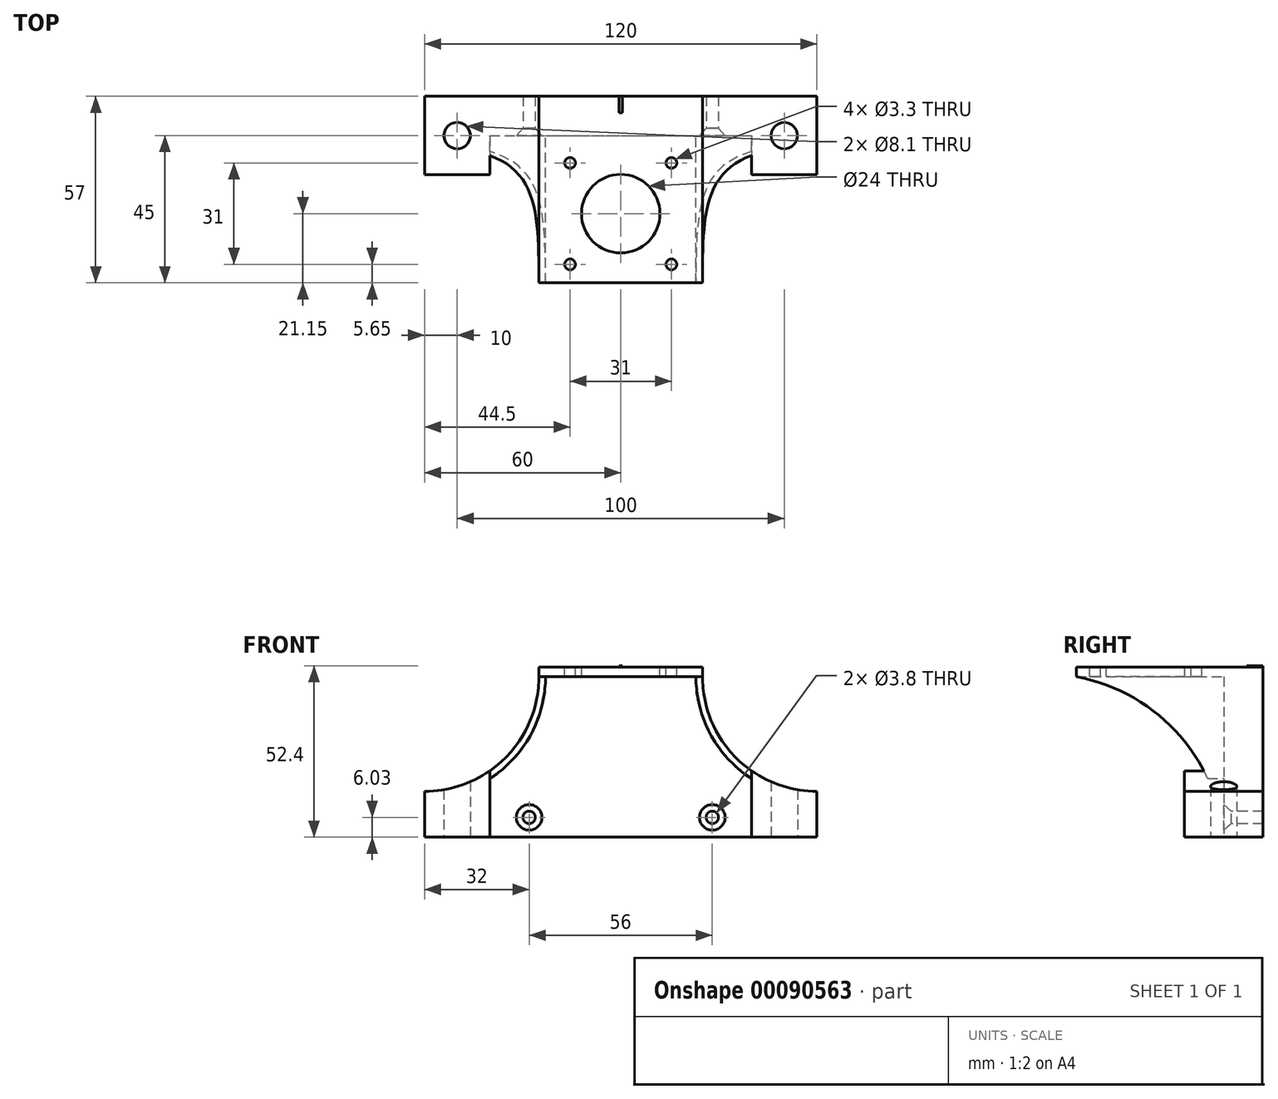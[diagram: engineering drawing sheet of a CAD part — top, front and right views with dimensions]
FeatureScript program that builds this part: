
annotation { "Feature Type Name" : "Feature", "Feature Type Description" : "" }
export const myFeature = defineFeature(function(context is Context, id is Id, definition is map)
    precondition{}
    {
        {
            var Q0;
            Q0=qCreatedBy(makeId("Front.planeOp"),FACE);
            var sketch = newSketch(context, id + "F0", { "sketchPlane" : qUnion([Q0])});
            skLineSegment(sketch, "E0.bottom", {"start": v(-27.18, 22.72) * mm, "end": v(22.82, 22.72) * mm});
            skLineSegment(sketch, "E0.top", {"start": v(-62.18, -29.28) * mm, "end": v(57.82, -29.28) * mm});
            skLineSegment(sketch, "E0.right", {"start": v(57.82, -15.28) * mm, "end": v(57.82, -29.28) * mm});
            skPoint(sketch, "E1", {"position": v(-2.18, 22.72) * mm});
            skLineSegment(sketch, "E2.top", {"start": v(-27.18, 19.72) * mm, "end": v(22.82, 19.72) * mm});
            skLineSegment(sketch, "E2.left", {"start": v(-27.18, 22.72) * mm, "end": v(-27.18, 19.72) * mm});
            skLineSegment(sketch, "E2.right", {"start": v(22.82, 22.72) * mm, "end": v(22.82, 19.72) * mm});
            skLineSegment(sketch, "E3", {"start": v(-62.18, -15.28) * mm, "end": v(57.82, -15.28) * mm, "construction": true});
            skArc(sketch, "E4", {"start": v(-62.18, -15.28) * mm, "mid": v(-37.43, -5.03) * mm, "end": v(-27.18, 19.72) * mm});
            skArc(sketch, "E5", {"start": v(22.82, 19.72) * mm, "mid": v(33.07, -5.03) * mm, "end": v(57.82, -15.28) * mm});
            skLineSegment(sketch, "E6.trimOffspring", {"start": v(-62.18, -15.28) * mm, "end": v(-62.18, -29.28) * mm});
            skPoint(sketch, "E0.left.start.orphan", {"position": v(-62.18, 22.72) * mm});
            skPoint(sketch, "E7.orphan", {"position": v(57.82, 22.72) * mm});
            skSolve(sketch);
        }
        {
            var Q0;
            Q0=makeQuery(id+"F0.imprint","IMPRINT",FACE,{"disambiguationData":[TD([[makeQuery(id+"F0.imprint","IMPRINT",EDGE,{"derivedFrom":sQuery(id+"F0.wireOp",EDGE,"E0.top")}),1.0]])]});
            var Q1;
            Q1=makeQuery(id+"F0.imprint","IMPRINT",FACE,{"disambiguationData":[TD([[makeQuery(id+"F0.imprint","IMPRINT",EDGE,{"derivedFrom":sQuery(id+"F0.wireOp",EDGE,"E0.bottom")}),-1.0]])]});
            extrude(context, id + "F1", {"entities" : qUnion([Q0, Q1]), "depth" : 12 * mm});
        }
        {
            var Q0;
            Q0=makeQuery(id+"F1.opExtrude","CAP_FACE",FACE,{"disambiguationData":[OSD([sQuery(id+"F0.wireOp",EDGE,"E0.top"),sQuery(id+"F0.wireOp",EDGE,"E0.right"),sQuery(id+"F0.wireOp",EDGE,"E0.bottom"),sQuery(id+"F0.wireOp",EDGE,"E2.left"),sQuery(id+"F0.wireOp",EDGE,"E2.right"),sQuery(id+"F0.wireOp",EDGE,"E4"),sQuery(id+"F0.wireOp",EDGE,"E5"),sQuery(id+"F0.wireOp",EDGE,"E6.trimOffspring")])],"isStart":false});
            var sketch = newSketch(context, id + "F2", { "sketchPlane" : qUnion([Q0])});
            skLineSegment(sketch, "E8", {"start": v(-27.18, 19.72) * mm, "end": v(22.82, 19.72) * mm});
            skArc(sketch, "E9.0", {"start": v(-60.18, -17.22) * mm, "mid": v(-35.32, -5.72) * mm, "end": v(-25.18, 19.72) * mm});
            skArc(sketch, "E10.0", {"start": v(20.82, 19.72) * mm, "mid": v(30.96, -5.72) * mm, "end": v(55.82, -17.22) * mm});
            skLineSegment(sketch, "E11.0", {"start": v(-60.18, -17.22) * mm, "end": v(-60.18, -29.28) * mm});
            skLineSegment(sketch, "E12.0", {"start": v(55.82, -17.22) * mm, "end": v(55.82, -29.28) * mm});
            skSolve(sketch);
        }
        {
            var Q0;
            Q0=qSketchRegion(id+"F2",true);
            var Q1;
            {var subQ2=sQuery(id+"F2.wireOp",EDGE,"E9.0");Q1=makeQuery(id+"F2.imprint","IMPRINT",FACE,{"disambiguationData":[TD([[makeQuery(id+"F2.imprint","IMPRINT",EDGE,{"derivedFrom":subQ2}),1.0]])]});}
            var Q2;
            Q2=makeQuery(id+"F2.imprint","IMPRINT",FACE,{"disambiguationData":[TD([[makeQuery(id+"F2.imprint","IMPRINT",EDGE,{"derivedFrom":makeQuery(id+"F1.opExtrude","CAP_EDGE",EDGE,{"disambiguationData":[OSD([sQuery(id+"F0.wireOp",EDGE,"E0.bottom")])],"isStart":false})}),-1.0]])]});
            var Q3;
            {var subQ2=sQuery(id+"F2.wireOp",EDGE,"E10.0");Q3=makeQuery(id+"F2.imprint","IMPRINT",FACE,{"disambiguationData":[TD([[makeQuery(id+"F2.imprint","IMPRINT",EDGE,{"derivedFrom":subQ2}),1.0]])]});}
            extrude(context, id + "F3", {"entities" : qUnion([Q0, Q1, Q2, Q3]), "operationType" : NewBodyOperationType.ADD, "depth" : 45 * mm});
        }
        {
            var Q0;
            {var subQ0=sQuery(id+"F0.wireOp",EDGE,"E6.trimOffspring");Q0=makeQuery(id+"F3.boolean.opBoolean","MERGE",FACE,{"derivedFrom":[makeQuery(id+"F1.opExtrude","SWEPT_FACE",FACE,{"disambiguationData":[OSD([subQ0])]}),makeQuery(id+"F3.opExtrude","SWEPT_FACE",FACE,{"disambiguationData":[OSD([subQ0])]})]});}
            var sketch = newSketch(context, id + "F4", { "sketchPlane" : qUnion([Q0])});
            skPoint(sketch, "E13.0", {"position": v(57, 19.72) * mm});
            skPoint(sketch, "E14.0", {"position": v(12, -29.28) * mm});
            skArc(sketch, "E15", {"start": v(57, 19.72) * mm, "mid": v(26.33, 2.73) * mm, "end": v(12, -29.28) * mm});
            skLineSegment(sketch, "E16.0", {"start": v(57, -15.28) * mm, "end": v(57, 19.72) * mm});
            skLineSegment(sketch, "E17.0", {"start": v(57, -15.28) * mm, "end": v(57, -29.28) * mm});
            skLineSegment(sketch, "E18.0", {"start": v(57, -29.28) * mm, "end": v(0, -29.28) * mm});
            skSolve(sketch);
        }
        {
            var Q0;
            Q0=qSketchRegion(id+"F4",true);
            extrude(context, id + "F5", {"entities" : qUnion([Q0]), "operationType" : NewBodyOperationType.REMOVE, "endBound" : BoundingType.THROUGH_ALL, "oppositeDirection" : true, "depth" : 25 * mm});
        }
        {
            var Q0;
            {var subQ0=sQuery(id+"F0.wireOp",EDGE,"E0.bottom");Q0=makeQuery(id+"F3.boolean.opBoolean","MERGE",FACE,{"derivedFrom":[makeQuery(id+"F1.opExtrude","SWEPT_FACE",FACE,{"disambiguationData":[OSD([subQ0])]}),makeQuery(id+"F3.opExtrude","SWEPT_FACE",FACE,{"disambiguationData":[OSD([subQ0])]})]});}
            var sketch = newSketch(context, id + "F6", { "sketchPlane" : qUnion([Q0])});
            skLineSegment(sketch, "E19", {"start": v(-2.18, -57) * mm, "end": v(-2.18, 0) * mm, "construction": true});
            skLineSegment(sketch, "E20", {"start": v(-27.18, -35.85) * mm, "end": v(22.82, -35.85) * mm, "construction": true});
            skCircle(sketch, "E21", {"center": v(-2.18, -35.85) * mm, "radius": 12 * mm});
            skLineSegment(sketch, "E22", {"start": v(-27.18, -51.35) * mm, "end": v(22.82, -51.35) * mm, "construction": true});
            skLineSegment(sketch, "E23", {"start": v(-17.68, 0) * mm, "end": v(-17.68, -57) * mm, "construction": true});
            skCircle(sketch, "E24", {"center": v(-17.68, -51.35) * mm, "radius": 1.65 * mm});
            skCircle(sketch, "E25.0.1.0", {"center": v(-17.68, -20.35) * mm, "radius": 1.65 * mm});
            skCircle(sketch, "E25.1.0.0", {"center": v(13.32, -51.35) * mm, "radius": 1.65 * mm});
            skCircle(sketch, "E25.1.1.0", {"center": v(13.32, -20.35) * mm, "radius": 1.65 * mm});
            skLineSegment(sketch, "E25.direction1", {"start": v(-17.68, -51.35) * mm, "end": v(13.32, -51.35) * mm, "construction": true});
            skLineSegment(sketch, "E25.direction2", {"start": v(-17.68, -51.35) * mm, "end": v(-17.68, -20.35) * mm, "construction": true});
            skSolve(sketch);
        }
        {
            var Q0;
            Q0=qSketchRegion(id+"F6",true);
            extrude(context, id + "F7", {"entities" : qUnion([Q0]), "operationType" : NewBodyOperationType.REMOVE, "oppositeDirection" : true, "depth" : 25 * mm});
        }
        {
            var Q0;
            Q0=makeQuery(id+"F1.opExtrude","CAP_FACE",FACE,{"disambiguationData":[OSD([sQuery(id+"F0.wireOp",EDGE,"E0.top"),sQuery(id+"F0.wireOp",EDGE,"E0.right"),sQuery(id+"F0.wireOp",EDGE,"E0.bottom"),sQuery(id+"F0.wireOp",EDGE,"E2.left"),sQuery(id+"F0.wireOp",EDGE,"E2.right"),sQuery(id+"F0.wireOp",EDGE,"E4"),sQuery(id+"F0.wireOp",EDGE,"E5"),sQuery(id+"F0.wireOp",EDGE,"E6.trimOffspring")])],"isStart":false});
            var sketch = newSketch(context, id + "F8", { "sketchPlane" : qUnion([Q0])});
            skLineSegment(sketch, "E26", {"start": v(-60.18, -23.25) * mm, "end": v(55.82, -23.25) * mm, "construction": true});
            skLineSegment(sketch, "E27", {"start": v(-30.18, -23.25) * mm, "end": v(-30.18, -29.28) * mm, "construction": true});
            skLineSegment(sketch, "E28", {"start": v(25.82, -23.25) * mm, "end": v(25.82, -29.28) * mm, "construction": true});
            skPoint(sketch, "E29", {"position": v(-30.18, -23.25) * mm});
            skPoint(sketch, "E30", {"position": v(25.82, -23.25) * mm});
            skSolve(sketch);
        }
        {
            var Q0;
            Q0=sQuery(id+"F8.wireOp",VERTEX,"E29");
            var Q1;
            Q1=sQuery(id+"F8.wireOp",VERTEX,"E30");
            var Q2;
            Q2=makeQuery(id+"F1.opExtrude","SWEPT_BODY",BODY,{"disambiguationData":[OSD([sQuery(id+"F0.wireOp",EDGE,"E0.top"),sQuery(id+"F0.wireOp",EDGE,"E0.right"),sQuery(id+"F0.wireOp",EDGE,"E0.bottom"),sQuery(id+"F0.wireOp",EDGE,"E2.left"),sQuery(id+"F0.wireOp",EDGE,"E2.right"),sQuery(id+"F0.wireOp",EDGE,"E4"),sQuery(id+"F0.wireOp",EDGE,"E5"),sQuery(id+"F0.wireOp",EDGE,"E6.trimOffspring")])]});
            hole(context, id + "F9", {"style" : HoleStyle.C_SINK, "endStyle" : HoleEndStyle.THROUGH, "standardTappedOrClearance" : lookupTablePath({ "standard" : "ANSI", "fit" : "Normal (ASME)", "size" : "#6", "type" : "Clearance" }), "standardBlindInLast" : lookupTablePath({ "fit" : "Free", "standard" : "ANSI", "size" : "#6", "type" : "Clearance" }), "holeDiameter" : 3.8 * mm, "cSinkDiameter" : 7.8 * mm, "cSinkAngle" : 82 * degree, "locations" : qUnion([Q0, Q1]), "scope" : qUnion([Q2]), "isTappedThrough" : true});
        }
        {
            var Q0;
            {var subQ0=sQuery(id+"F0.wireOp",EDGE,"E0.bottom");Q0=makeQuery(id+"F3.boolean.opBoolean","MERGE",FACE,{"derivedFrom":[makeQuery(id+"F1.opExtrude","SWEPT_FACE",FACE,{"disambiguationData":[OSD([subQ0])]}),makeQuery(id+"F3.opExtrude","SWEPT_FACE",FACE,{"disambiguationData":[OSD([subQ0])]})]});}
            var sketch = newSketch(context, id + "F10", { "sketchPlane" : qUnion([Q0])});
            skPoint(sketch, "E31", {"position": v(-2.18, 0) * mm});
            skLineSegment(sketch, "E32.bottom", {"start": v(-2.68, -5) * mm, "end": v(-1.68, -5) * mm});
            skLineSegment(sketch, "E32.top", {"start": v(-2.68, 0) * mm, "end": v(-1.68, 0) * mm});
            skLineSegment(sketch, "E32.left", {"start": v(-2.68, -5) * mm, "end": v(-2.68, 0) * mm});
            skLineSegment(sketch, "E32.right", {"start": v(-1.68, -5) * mm, "end": v(-1.68, 0) * mm});
            skPoint(sketch, "E33", {"position": v(-2.18, -5) * mm});
            skSolve(sketch);
        }
        {
            var Q0;
            Q0=qSketchRegion(id+"F10",true);
            extrude(context, id + "F11", {"entities" : qUnion([Q0]), "operationType" : NewBodyOperationType.ADD, "depth" : 0.4 * mm});
        }
        {
            var Q0;
            {var subQ0=sQuery(id+"F0.wireOp",EDGE,"E0.top");var subQ1=makeQuery(id+"F1.opExtrude","CAP_EDGE",EDGE,{"disambiguationData":[OSD([subQ0])],"isStart":false});Q0=makeQuery(id+"F3.boolean.opBoolean","MERGE",FACE,{"derivedFrom":[makeQuery(id+"F1.opExtrude","SWEPT_FACE",FACE,{"disambiguationData":[OSD([subQ0])]}),makeQuery(id+"F3.opExtrude","SWEPT_FACE",FACE,{"disambiguationData":[OSD([subQ0]),TDD([makeQuery(id+"F2.imprint","IMPRINT",EDGE,{"disambiguationData":[TD([[makeQuery(id+"F2.imprint","INTERSECT",VERTEX,{"derivedFrom":[subQ1,makeQuery(id+"F1.opExtrude","CAP_EDGE",EDGE,{"disambiguationData":[OSD([sQuery(id+"F0.wireOp",EDGE,"E6.trimOffspring")])],"isStart":false})]}),-1.0]])],"derivedFrom":subQ1})])]}),makeQuery(id+"F3.opExtrude","SWEPT_FACE",FACE,{"disambiguationData":[OSD([subQ0]),TDD([makeQuery(id+"F2.imprint","IMPRINT",EDGE,{"disambiguationData":[TD([[makeQuery(id+"F2.imprint","INTERSECT",VERTEX,{"derivedFrom":[subQ1,makeQuery(id+"F1.opExtrude","CAP_EDGE",EDGE,{"disambiguationData":[OSD([sQuery(id+"F0.wireOp",EDGE,"E0.right")])],"isStart":false})]}),1.0]])],"derivedFrom":subQ1})])]})]});}
            var sketch = newSketch(context, id + "F12", { "sketchPlane" : qUnion([Q0])});
            skLineSegment(sketch, "E34", {"start": v(-52.18, 0) * mm, "end": v(-52.18, 12) * mm, "construction": true});
            skLineSegment(sketch, "E35", {"start": v(47.82, 0) * mm, "end": v(47.82, 12) * mm, "construction": true});
            skLineSegment(sketch, "E36.bottom", {"start": v(-62.18, 0) * mm, "end": v(-42.18, 0) * mm});
            skLineSegment(sketch, "E36.top", {"start": v(-62.18, 24) * mm, "end": v(-42.18, 24) * mm});
            skLineSegment(sketch, "E36.left", {"start": v(-62.18, 0) * mm, "end": v(-62.18, 24) * mm});
            skLineSegment(sketch, "E36.right", {"start": v(-42.18, 0) * mm, "end": v(-42.18, 24) * mm});
            skCircle(sketch, "E37", {"center": v(-52.18, 12) * mm, "radius": 4.05 * mm});
            skLineSegment(sketch, "E38.bottom", {"start": v(57.82, 0) * mm, "end": v(37.82, 0) * mm});
            skLineSegment(sketch, "E38.top", {"start": v(57.82, 24) * mm, "end": v(37.82, 24) * mm});
            skLineSegment(sketch, "E38.left", {"start": v(57.82, 0) * mm, "end": v(57.82, 24) * mm});
            skLineSegment(sketch, "E38.right", {"start": v(37.82, 0) * mm, "end": v(37.82, 24) * mm});
            skCircle(sketch, "E39", {"center": v(47.82, 12) * mm, "radius": 4.05 * mm});
            skSolve(sketch);
        }
        {
            var Q0;
            {var subQ6=sQuery(id+"F12.wireOp",EDGE,"E36.top");Q0=makeQuery(id+"F12.imprint","IMPRINT",FACE,{"disambiguationData":[TD([[makeQuery(id+"F12.imprint","IMPRINT",EDGE,{"derivedFrom":subQ6}),-1.0]])]});}
            var Q1;
            {var subQ0=sQuery(id+"F12.wireOp",EDGE,"E37");var subQ1=makeQuery(id+"F1.opExtrude","CAP_EDGE",EDGE,{"disambiguationData":[OSD([sQuery(id+"F0.wireOp",EDGE,"E0.top")])],"isStart":false});var subQ2=makeQuery(id+"F12.imprint","INTERSECT",VERTEX,{"disambiguationData":[OD(0.0)],"derivedFrom":[subQ1,subQ0]});Q1=makeQuery(id+"F12.imprint","IMPRINT",FACE,{"disambiguationData":[TD([[makeQuery(id+"F12.imprint","IMPRINT",EDGE,{"disambiguationData":[TD([[subQ2,1.0]])],"derivedFrom":subQ0}),1.0]])]});}
            var Q2;
            {var subQ0=sQuery(id+"F0.wireOp",EDGE,"E4");Q2=makeQuery(id+"F3.boolean.opBoolean","MERGE",FACE,{"derivedFrom":[makeQuery(id+"F1.opExtrude","SWEPT_FACE",FACE,{"disambiguationData":[OSD([subQ0])]}),makeQuery(id+"F3.opExtrude","SWEPT_FACE",FACE,{"disambiguationData":[OSD([subQ0])]})]});}
            extrude(context, id + "F13", {"entities" : qUnion([Q0, Q1]), "operationType" : NewBodyOperationType.ADD, "endBound" : BoundingType.UP_TO_SURFACE, "oppositeDirection" : true, "endBoundEntityFace" : qUnion([Q2]), "depth" : 25 * mm});
        }
        {
            var Q0;
            {var subQ6=sQuery(id+"F12.wireOp",EDGE,"E38.top");Q0=makeQuery(id+"F12.imprint","IMPRINT",FACE,{"disambiguationData":[TD([[makeQuery(id+"F12.imprint","IMPRINT",EDGE,{"derivedFrom":subQ6}),1.0]])]});}
            var Q1;
            {var subQ0=sQuery(id+"F12.wireOp",EDGE,"E39");var subQ1=makeQuery(id+"F1.opExtrude","CAP_EDGE",EDGE,{"disambiguationData":[OSD([sQuery(id+"F0.wireOp",EDGE,"E0.top")])],"isStart":false});var subQ2=makeQuery(id+"F12.imprint","INTERSECT",VERTEX,{"disambiguationData":[OD(0.0)],"derivedFrom":[subQ1,subQ0]});Q1=makeQuery(id+"F12.imprint","IMPRINT",FACE,{"disambiguationData":[TD([[makeQuery(id+"F12.imprint","IMPRINT",EDGE,{"disambiguationData":[TD([[subQ2,-1.0]])],"derivedFrom":subQ0}),1.0]])]});}
            var Q2;
            {var subQ0=sQuery(id+"F0.wireOp",EDGE,"E5");Q2=makeQuery(id+"F3.boolean.opBoolean","MERGE",FACE,{"derivedFrom":[makeQuery(id+"F1.opExtrude","SWEPT_FACE",FACE,{"disambiguationData":[OSD([subQ0])]}),makeQuery(id+"F3.opExtrude","SWEPT_FACE",FACE,{"disambiguationData":[OSD([subQ0])]})]});}
            extrude(context, id + "F14", {"entities" : qUnion([Q0, Q1]), "operationType" : NewBodyOperationType.ADD, "endBound" : BoundingType.UP_TO_SURFACE, "oppositeDirection" : true, "endBoundEntityFace" : qUnion([Q2]), "depth" : 25 * mm});
        }
        {
            var Q0;
            {var subQ0=sQuery(id+"F12.wireOp",EDGE,"E37");var subQ1=makeQuery(id+"F1.opExtrude","CAP_EDGE",EDGE,{"disambiguationData":[OSD([sQuery(id+"F0.wireOp",EDGE,"E0.top")])],"isStart":false});var subQ2=makeQuery(id+"F12.imprint","INTERSECT",VERTEX,{"disambiguationData":[OD(0.0)],"derivedFrom":[subQ1,subQ0]});Q0=makeQuery(id+"F12.imprint","IMPRINT",FACE,{"disambiguationData":[TD([[makeQuery(id+"F12.imprint","IMPRINT",EDGE,{"disambiguationData":[TD([[subQ2,1.0]])],"derivedFrom":subQ0}),1.0]])]});}
            var Q1;
            {var subQ0=sQuery(id+"F12.wireOp",EDGE,"E37");var subQ1=makeQuery(id+"F1.opExtrude","CAP_EDGE",EDGE,{"disambiguationData":[OSD([sQuery(id+"F0.wireOp",EDGE,"E0.top")])],"isStart":false});var subQ2=makeQuery(id+"F12.imprint","INTERSECT",VERTEX,{"disambiguationData":[OD(0.0)],"derivedFrom":[subQ1,subQ0]});Q1=makeQuery(id+"F12.imprint","IMPRINT",FACE,{"disambiguationData":[TD([[makeQuery(id+"F12.imprint","IMPRINT",EDGE,{"disambiguationData":[TD([[subQ2,-1.0]])],"derivedFrom":subQ0}),1.0]])]});}
            var Q2;
            {var subQ0=sQuery(id+"F12.wireOp",EDGE,"E39");var subQ1=makeQuery(id+"F1.opExtrude","CAP_EDGE",EDGE,{"disambiguationData":[OSD([sQuery(id+"F0.wireOp",EDGE,"E0.top")])],"isStart":false});var subQ2=makeQuery(id+"F12.imprint","INTERSECT",VERTEX,{"disambiguationData":[OD(0.0)],"derivedFrom":[subQ1,subQ0]});Q2=makeQuery(id+"F12.imprint","IMPRINT",FACE,{"disambiguationData":[TD([[makeQuery(id+"F12.imprint","IMPRINT",EDGE,{"disambiguationData":[TD([[subQ2,-1.0]])],"derivedFrom":subQ0}),1.0]])]});}
            var Q3;
            {var subQ0=sQuery(id+"F12.wireOp",EDGE,"E39");var subQ1=makeQuery(id+"F1.opExtrude","CAP_EDGE",EDGE,{"disambiguationData":[OSD([sQuery(id+"F0.wireOp",EDGE,"E0.top")])],"isStart":false});var subQ2=makeQuery(id+"F12.imprint","INTERSECT",VERTEX,{"disambiguationData":[OD(0.0)],"derivedFrom":[subQ1,subQ0]});Q3=makeQuery(id+"F12.imprint","IMPRINT",FACE,{"disambiguationData":[TD([[makeQuery(id+"F12.imprint","IMPRINT",EDGE,{"disambiguationData":[TD([[subQ2,1.0]])],"derivedFrom":subQ0}),1.0]])]});}
            extrude(context, id + "F15", {"entities" : qUnion([Q0, Q1, Q2, Q3]), "operationType" : NewBodyOperationType.REMOVE, "oppositeDirection" : true, "depth" : 25 * mm});
        }
    });
